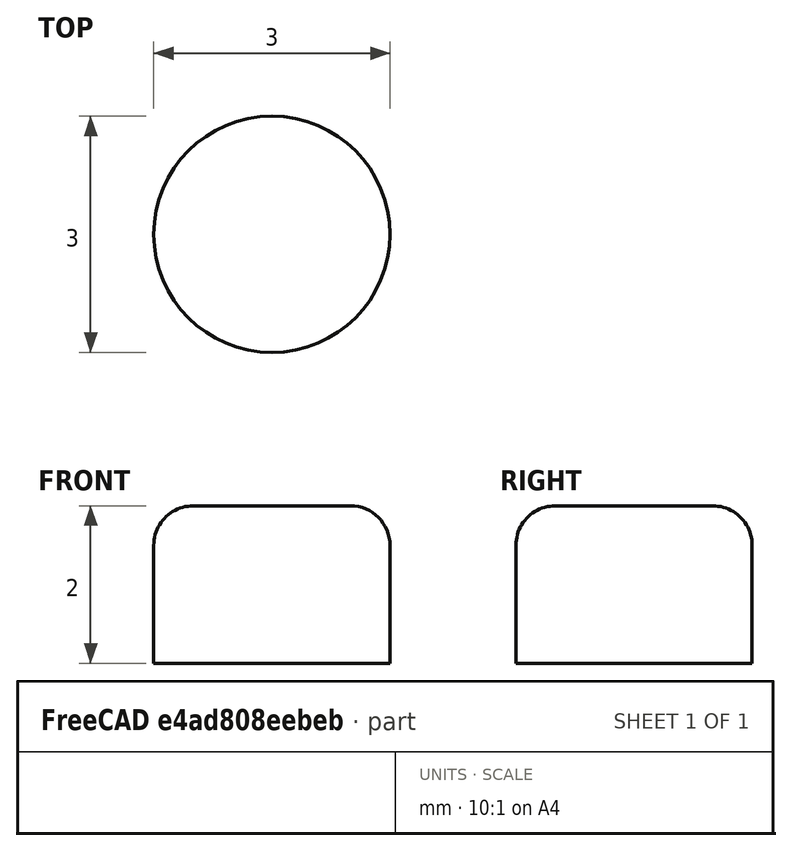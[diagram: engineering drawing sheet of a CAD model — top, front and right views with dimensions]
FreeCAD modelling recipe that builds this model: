
FCSTD DOCUMENT  (FreeCAD 1.0R39109 (Git))
Label: Stopper2
License: All rights reserved
LicenseURL: https://en.wikipedia.org/wiki/All_rights_reserved
objects: Sketcher::SketchObject×1, PartDesign::Pad×1, PartDesign::Fillet×1, PartDesign::Body×1
note: 9 computed .brp shape members not serialized (recipe doc carries the construction recipe); baked Part::Feature solids carry a one-line shape summary decoded from their .brp

FEATURE [Sketcher::SketchObject] Sketch
  ArcFitTolerance = 1e-06
  AttachmentSupport = -> [XY_Plane]
  FullyConstrained = true
  MakeInternals = false
  MapMode = 5
  sketch-geometry (1):
    g0: Circle CenterX=0 CenterY=0 CenterZ=0 NormalX=0 NormalY=0 NormalZ=1 AngleXU=0 Radius=1.5
  constraints (2):
    c: Coincident(g0,g-1)
    c: Diameter(g0) = 3
FEATURE [PartDesign::Pad] Pad
  Direction = (0,0,1)
  Length = 2
  Length2 = 10
  Profile = -> Sketch
  ReferenceAxis = -> Sketch [N_Axis]
  Refine = true
  Suppressed = false
  Type = 0
FEATURE [PartDesign::Fillet] Fillet
  Base = -> Pad [Edge3]
  BaseFeature = -> Pad
  Radius = 0.5
  Refine = true
  SupportTransform = false
  Suppressed = false
  UseAllEdges = false
FEATURE [PartDesign::Body] Body
  AllowCompound = false
  Group = -> [Sketch,Pad,Fillet]
  Origin = -> Origin
  Tip = -> Fillet
